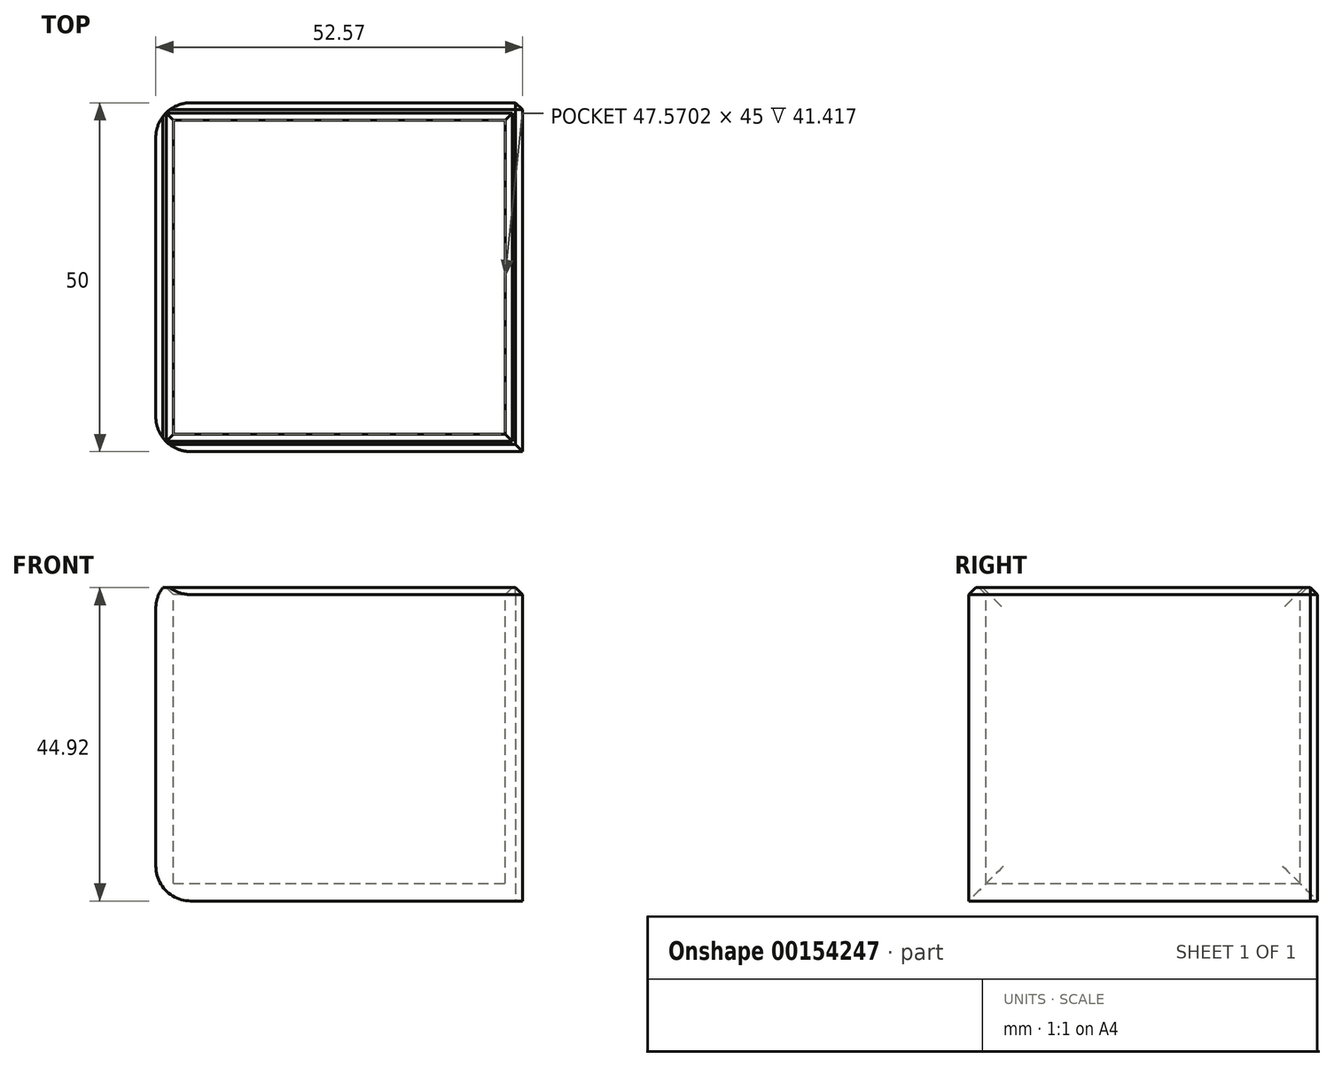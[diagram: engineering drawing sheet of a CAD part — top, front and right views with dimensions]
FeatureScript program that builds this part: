
annotation { "Feature Type Name" : "Feature", "Feature Type Description" : "" }
export const myFeature = defineFeature(function(context is Context, id is Id, definition is map)
    precondition{}
    {
        {
            var Q0;
            Q0=qCreatedBy(makeId("Front.planeOp"),FACE);
            var sketch = newSketch(context, id + "F0", { "sketchPlane" : qUnion([Q0])});
            skLineSegment(sketch, "E0.bottom", {"start": v(0, 0) * mm, "end": v(52.57, 0) * mm});
            skLineSegment(sketch, "E0.top", {"start": v(0, 44.92) * mm, "end": v(52.57, 44.92) * mm});
            skLineSegment(sketch, "E0.left", {"start": v(0, 0) * mm, "end": v(0, 44.92) * mm});
            skLineSegment(sketch, "E0.right", {"start": v(52.57, 0) * mm, "end": v(52.57, 44.92) * mm});
            skSolve(sketch);
        }
        {
            var Q0;
            Q0 = qSketchRegion(id + "F0", true);
            extrude(context, id + "F1", {"entities" : qUnion([Q0]), "depth" : 25 * mm});
        }
        {
            var Q0;
            Q0=makeQuery(id+"F1.opExtrude","CAP_FACE",FACE,{"disambiguationData":[OSD([sQuery(id+"F0.wireOp",EDGE,"E0.bottom"),sQuery(id+"F0.wireOp",EDGE,"E0.top"),sQuery(id+"F0.wireOp",EDGE,"E0.left"),sQuery(id+"F0.wireOp",EDGE,"E0.right")])],"isStart":false});
            extrude(context, id + "F2", {"entities" : qUnion([Q0]), "operationType" : NewBodyOperationType.ADD, "depth" : 25 * mm});
        }
        {
            var Q0;
            {var subQ0=sQuery(id+"F0.wireOp",EDGE,"E0.top");Q0=makeQuery(id+"F2.boolean.opBoolean","MERGE",FACE,{"derivedFrom":[makeQuery(id+"F1.opExtrude","SWEPT_FACE",FACE,{"disambiguationData":[OSD([subQ0])]}),makeQuery(id+"F2.opExtrude","SWEPT_FACE",FACE,{"disambiguationData":[OSD([subQ0])]})]});}
            shell(context, id + "F3", {"entities" : qUnion([Q0]), "thickness" : 2.5 * mm});
        }
        {
            var Q0;
            Q0=makeQuery(id+"F1.opExtrude","CAP_EDGE",EDGE,{"disambiguationData":[OSD([sQuery(id+"F0.wireOp",EDGE,"E0.right")])],"isStart":true});
            var Q1;
            {var subQ0=sQuery(id+"F0.wireOp",EDGE,"E0.top");Q1=makeQuery(id+"F2.boolean.opBoolean","MERGE",FACE,{"derivedFrom":[makeQuery(id+"F1.opExtrude","SWEPT_FACE",FACE,{"disambiguationData":[OSD([subQ0])]}),makeQuery(id+"F2.opExtrude","SWEPT_FACE",FACE,{"disambiguationData":[OSD([subQ0])]})]});}
            chamfer(context, id + "F4", {"entities" : qUnion([Q0, Q1]), "width" : 1 * mm, "tangentPropagation" : true});
        }
        {
            var Q0;
            {var subQ0=sQuery(id+"F0.wireOp",EDGE,"E0.left");Q0=makeQuery(id+"F2.boolean.opBoolean","MERGE",FACE,{"derivedFrom":[makeQuery(id+"F1.opExtrude","SWEPT_FACE",FACE,{"disambiguationData":[OSD([subQ0])]}),makeQuery(id+"F2.opExtrude","SWEPT_FACE",FACE,{"disambiguationData":[OSD([subQ0])]})]});}
            fillet(context, id + "F5", {"entities" : qUnion([Q0]), "radius" : 5 * mm, "tangentPropagation" : true, "allowEdgeOverflow" : false});
        }
    });
